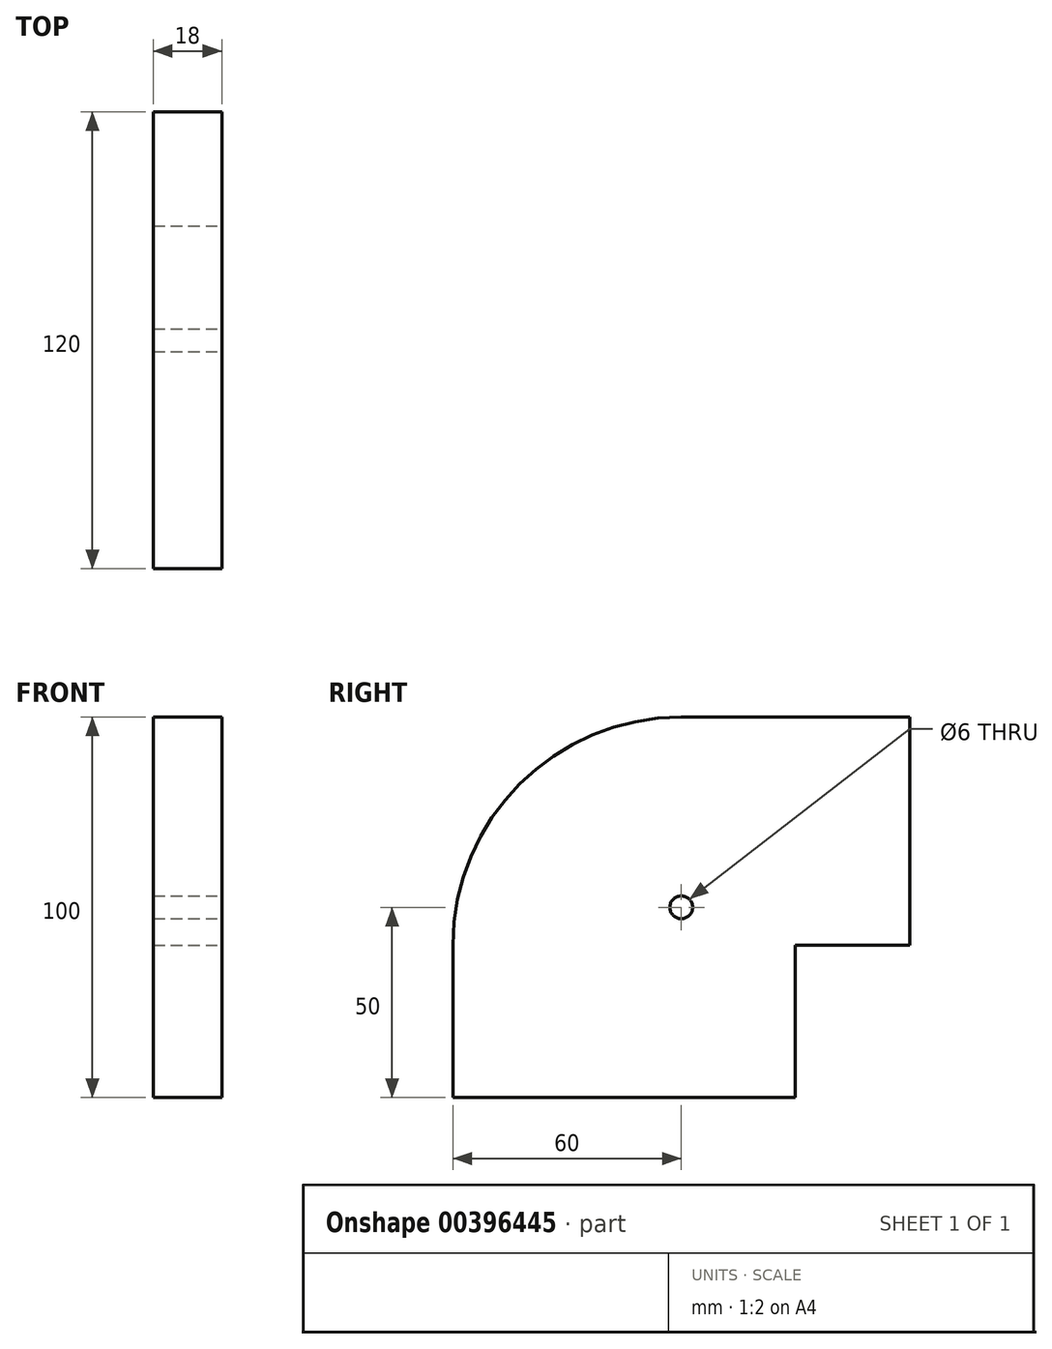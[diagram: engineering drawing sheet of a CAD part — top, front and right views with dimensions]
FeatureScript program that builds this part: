
annotation { "Feature Type Name" : "Feature", "Feature Type Description" : "" }
export const myFeature = defineFeature(function(context is Context, id is Id, definition is map)
    precondition{}
    {
        {
            var Q0;
            Q0=qCreatedBy(makeId("Right.planeOp"),FACE);
            var sketch = newSketch(context, id + "F0", { "sketchPlane" : qUnion([Q0])});
            skLineSegment(sketch, "E0.bottom", {"start": v(0, 0) * mm, "end": v(-120, 0) * mm});
            skLineSegment(sketch, "E0.top", {"start": v(0, 100) * mm, "end": v(-120, 100) * mm});
            skLineSegment(sketch, "E0.left", {"start": v(0, 0) * mm, "end": v(0, 100) * mm});
            skLineSegment(sketch, "E0.right", {"start": v(-120, 0) * mm, "end": v(-120, 100) * mm});
            skSolve(sketch);
        }
        {
            var Q0;
            Q0=makeQuery(id+"F0.imprint","IMPRINT",FACE,{"disambiguationData":[TD([[makeQuery(id+"F0.imprint","IMPRINT",EDGE,{"derivedFrom":sQuery(id+"F0.wireOp",EDGE,"E0.bottom")}),-1.0]])]});
            extrude(context, id + "F1", {"entities" : qUnion([Q0]), "depth" : 18 * mm});
        }
        {
            var Q0;
            Q0=makeQuery(id+"F1.opExtrude","CAP_FACE",FACE,{"disambiguationData":[OSD([sQuery(id+"F0.wireOp",EDGE,"E0.bottom"),sQuery(id+"F0.wireOp",EDGE,"E0.top"),sQuery(id+"F0.wireOp",EDGE,"E0.left"),sQuery(id+"F0.wireOp",EDGE,"E0.right")])],"isStart":false});
            var sketch = newSketch(context, id + "F2", { "sketchPlane" : qUnion([Q0])});
            skPoint(sketch, "E1", {"position": v(-60, 50) * mm});
            skSolve(sketch);
        }
        {
            var Q0;
            Q0=sQuery(id+"F2.wireOp",VERTEX,"E1");
            var Q1;
            Q1=makeQuery(id+"F1.opExtrude","SWEPT_BODY",BODY,{"disambiguationData":[OSD([sQuery(id+"F0.wireOp",EDGE,"E0.bottom"),sQuery(id+"F0.wireOp",EDGE,"E0.top"),sQuery(id+"F0.wireOp",EDGE,"E0.left"),sQuery(id+"F0.wireOp",EDGE,"E0.right")])]});
            hole(context, id + "F3", {"style" : HoleStyle.SIMPLE, "endStyle" : HoleEndStyle.THROUGH, "holeDiameter" : 6 * mm, "isTappedThrough" : true, "tappedDepth" : 12 * mm, "tapClearance" : 3, "locations" : qUnion([Q0]), "scope" : qUnion([Q1])});
        }
        {
            var Q0;
            Q0=makeQuery(id+"F1.opExtrude","SWEPT_EDGE",EDGE,{"disambiguationData":[OSD([sQuery(id+"F0.wireOp",EDGE,"E0.top"),sQuery(id+"F0.wireOp",EDGE,"E0.right")])]});
            fillet(context, id + "F4", {"entities" : qUnion([Q0]), "radius" : 60 * mm, "tangentPropagation" : true, "allowEdgeOverflow" : false});
        }
        {
            var Q0;
            Q0=makeQuery(id+"F1.opExtrude","CAP_FACE",FACE,{"disambiguationData":[OSD([sQuery(id+"F0.wireOp",EDGE,"E0.bottom"),sQuery(id+"F0.wireOp",EDGE,"E0.top"),sQuery(id+"F0.wireOp",EDGE,"E0.left"),sQuery(id+"F0.wireOp",EDGE,"E0.right")])],"isStart":false});
            var sketch = newSketch(context, id + "F5", { "sketchPlane" : qUnion([Q0])});
            skLineSegment(sketch, "E2.bottom", {"start": v(0, 0) * mm, "end": v(-30, 0) * mm});
            skLineSegment(sketch, "E2.top", {"start": v(0, 40) * mm, "end": v(-30, 40) * mm});
            skLineSegment(sketch, "E2.left", {"start": v(0, 0) * mm, "end": v(0, 40) * mm});
            skLineSegment(sketch, "E2.right", {"start": v(-30, 0) * mm, "end": v(-30, 40) * mm});
            skSolve(sketch);
        }
        {
            var Q0;
            Q0=makeQuery(id+"F5.imprint","IMPRINT",FACE,{"disambiguationData":[TD([[makeQuery(id+"F5.imprint","IMPRINT",EDGE,{"derivedFrom":sQuery(id+"F5.wireOp",EDGE,"E2.bottom")}),-1.0]])]});
            extrude(context, id + "F6", {"entities" : qUnion([Q0]), "operationType" : NewBodyOperationType.REMOVE, "endBound" : BoundingType.UP_TO_NEXT, "oppositeDirection" : true, "depth" : 25 * mm});
        }
    });
